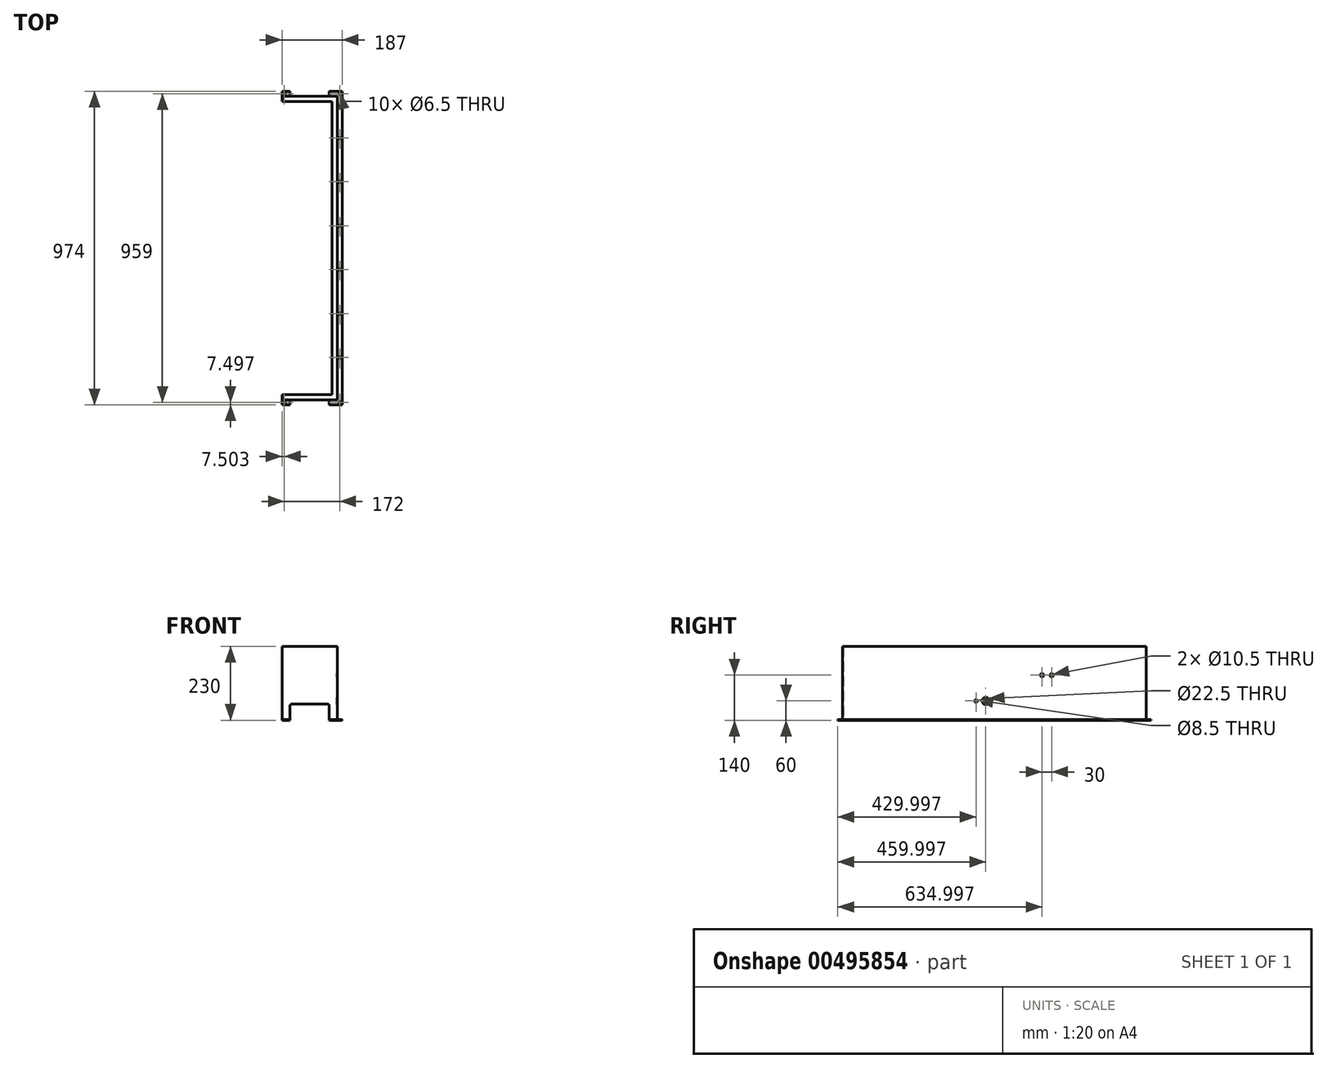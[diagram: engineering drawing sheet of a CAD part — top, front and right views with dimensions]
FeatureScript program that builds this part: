
annotation { "Feature Type Name" : "Feature", "Feature Type Description" : "" }
export const myFeature = defineFeature(function(context is Context, id is Id, definition is map)
    precondition{}
    {
        {
            var Q0;
            Q0=qCreatedBy(makeId("Top.planeOp"),FACE);
            var sketch = newSketch(context, id + "F0", { "sketchPlane" : qUnion([Q0])});
            skLineSegment(sketch, "E0", {"start": v(-19.6, 942) * mm, "end": v(150.4, 942) * mm});
            skLineSegment(sketch, "E1", {"start": v(150.4, 942) * mm, "end": v(150.4, 2) * mm});
            skLineSegment(sketch, "E2", {"start": v(150.4, 2) * mm, "end": v(-19.6, 2) * mm});
            skLineSegment(sketch, "E3", {"start": v(-19.6, 2) * mm, "end": v(-19.6, -15) * mm});
            skLineSegment(sketch, "E4", {"start": v(-19.6, -15) * mm, "end": v(167.4, -15) * mm});
            skLineSegment(sketch, "E5", {"start": v(167.4, -15) * mm, "end": v(167.4, 959) * mm});
            skLineSegment(sketch, "E6", {"start": v(167.4, 959) * mm, "end": v(-19.6, 959) * mm});
            skLineSegment(sketch, "E7", {"start": v(-19.6, 959) * mm, "end": v(-19.6, 942) * mm});
            skCircle(sketch, "E8", {"center": v(-12.1, 951.5) * mm, "radius": 3.25 * mm});
            skCircle(sketch, "E9", {"center": v(159.9, 951.5) * mm, "radius": 3.25 * mm});
            skCircle(sketch, "E10", {"center": v(-12.1, -7.5) * mm, "radius": 3.25 * mm});
            skCircle(sketch, "E11", {"center": v(159.9, -7.5) * mm, "radius": 3.25 * mm});
            skCircle(sketch, "E12.0.1.0", {"center": v(159.9, 814.9) * mm, "radius": 3.25 * mm});
            skCircle(sketch, "E12.0.2.0", {"center": v(159.9, 678.3) * mm, "radius": 3.25 * mm});
            skCircle(sketch, "E12.0.3.0", {"center": v(159.9, 541.7) * mm, "radius": 3.25 * mm});
            skCircle(sketch, "E12.0.4.0", {"center": v(159.9, 405.1) * mm, "radius": 3.25 * mm});
            skCircle(sketch, "E12.0.5.0", {"center": v(159.9, 268.5) * mm, "radius": 3.25 * mm});
            skCircle(sketch, "E12.0.6.0", {"center": v(159.9, 131.9) * mm, "radius": 3.25 * mm});
            skLineSegment(sketch, "E12.direction1", {"start": v(159.9, 951.5) * mm, "end": v(184.9, 951.5) * mm, "construction": true});
            skLineSegment(sketch, "E12.direction2", {"start": v(159.9, 951.5) * mm, "end": v(159.9, 814.9) * mm, "construction": true});
            skSolve(sketch);
        }
        {
            var Q0;
            Q0=qSketchRegion(id+"F0",true);
            extrude(context, id + "F1", {"entities" : qUnion([Q0]), "depth" : 2 * mm});
        }
        {
            var Q0;
            Q0=makeQuery(id+"F1.opExtrude","CAP_FACE",FACE,{"disambiguationData":[OSD([sQuery(id+"F0.wireOp",EDGE,"E0"),sQuery(id+"F0.wireOp",EDGE,"E1"),sQuery(id+"F0.wireOp",EDGE,"E2"),sQuery(id+"F0.wireOp",EDGE,"E3"),sQuery(id+"F0.wireOp",EDGE,"E4"),sQuery(id+"F0.wireOp",EDGE,"E5"),sQuery(id+"F0.wireOp",EDGE,"E6"),sQuery(id+"F0.wireOp",EDGE,"E7")])],"isStart":false});
            var sketch = newSketch(context, id + "F2", { "sketchPlane" : qUnion([Q0])});
            skLineSegment(sketch, "E13.0", {"start": v(-19.6, 942) * mm, "end": v(150.4, 942) * mm});
            skLineSegment(sketch, "E14.0", {"start": v(150.4, 942) * mm, "end": v(150.4, 2) * mm});
            skLineSegment(sketch, "E15.0", {"start": v(150.4, 2) * mm, "end": v(-19.6, 2) * mm});
            skLineSegment(sketch, "E16.0", {"start": v(152.4, 0) * mm, "end": v(-19.6, 0) * mm});
            skLineSegment(sketch, "E16.1", {"start": v(152.4, 944) * mm, "end": v(152.4, 0) * mm});
            skLineSegment(sketch, "E16.2", {"start": v(-19.6, 944) * mm, "end": v(152.4, 944) * mm});
            skLineSegment(sketch, "E17", {"start": v(-19.6, 0) * mm, "end": v(-19.6, 2) * mm});
            skLineSegment(sketch, "E18", {"start": v(-19.6, 944) * mm, "end": v(-19.6, 942) * mm});
            skSolve(sketch);
        }
        {
            var Q0;
            Q0=qSketchRegion(id+"F2",true);
            extrude(context, id + "F3", {"entities" : qUnion([Q0]), "operationType" : NewBodyOperationType.ADD, "depth" : 226 * mm});
        }
        {
            var Q0;
            Q0=makeQuery(id+"F3.opExtrude","CAP_FACE",FACE,{"disambiguationData":[OSD([sQuery(id+"F2.wireOp",EDGE,"E13.0"),sQuery(id+"F2.wireOp",EDGE,"E14.0"),sQuery(id+"F2.wireOp",EDGE,"E15.0"),sQuery(id+"F2.wireOp",EDGE,"E16.0"),sQuery(id+"F2.wireOp",EDGE,"E16.1"),sQuery(id+"F2.wireOp",EDGE,"E16.2"),sQuery(id+"F2.wireOp",EDGE,"E17"),sQuery(id+"F2.wireOp",EDGE,"E18")])],"isStart":false});
            var sketch = newSketch(context, id + "F4", { "sketchPlane" : qUnion([Q0])});
            skLineSegment(sketch, "E19.0", {"start": v(-19.6, 944) * mm, "end": v(152.4, 944) * mm});
            skLineSegment(sketch, "E20.0", {"start": v(152.4, 944) * mm, "end": v(152.4, 0) * mm});
            skLineSegment(sketch, "E21.0", {"start": v(152.4, 0) * mm, "end": v(-19.6, 0) * mm});
            skLineSegment(sketch, "E22.0", {"start": v(135.4, 17) * mm, "end": v(-19.6, 17) * mm});
            skLineSegment(sketch, "E22.1", {"start": v(135.4, 927) * mm, "end": v(135.4, 17) * mm});
            skLineSegment(sketch, "E22.2", {"start": v(-19.6, 927) * mm, "end": v(135.4, 927) * mm});
            skLineSegment(sketch, "E23", {"start": v(-19.6, 17) * mm, "end": v(-19.6, 0) * mm});
            skLineSegment(sketch, "E24", {"start": v(-19.6, 944) * mm, "end": v(-19.6, 927) * mm});
            skSolve(sketch);
        }
        {
            var Q0;
            Q0=qSketchRegion(id+"F4",true);
            extrude(context, id + "F5", {"entities" : qUnion([Q0]), "operationType" : NewBodyOperationType.ADD, "depth" : 2 * mm});
        }
        {
            var Q0;
            Q0=makeQuery(id+"F1.opExtrude","SWEPT_FACE",FACE,{"disambiguationData":[OSD([sQuery(id+"F0.wireOp",EDGE,"E6")])]});
            var sketch = newSketch(context, id + "F6", { "sketchPlane" : qUnion([Q0])});
            skLineSegment(sketch, "E25.bottom", {"start": v(-122.4, 50) * mm, "end": v(-10.4, 50) * mm});
            skLineSegment(sketch, "E25.top", {"start": v(-127.4, -20.45) * mm, "end": v(-5.4, -20.45) * mm});
            skLineSegment(sketch, "E25.left", {"start": v(-127.4, 45) * mm, "end": v(-127.4, -20.45) * mm});
            skLineSegment(sketch, "E25.right", {"start": v(-5.4, 45) * mm, "end": v(-5.4, -20.45) * mm});
            skPoint(sketch, "E26.visualSharp", {"position": v(-127.4, 50) * mm});
            skArc(sketch, "E26.filletArc", {"start": v(-122.4, 50) * mm, "mid": v(-125.93, 48.54) * mm, "end": v(-127.4, 45) * mm});
            skPoint(sketch, "E27.visualSharp", {"position": v(-5.4, 50) * mm});
            skArc(sketch, "E27.filletArc", {"start": v(-5.4, 45) * mm, "mid": v(-6.86, 48.54) * mm, "end": v(-10.4, 50) * mm});
            skSolve(sketch);
        }
        {
            var Q0;
            Q0=qSketchRegion(id+"F6",true);
            extrude(context, id + "F7", {"entities" : qUnion([Q0]), "operationType" : NewBodyOperationType.REMOVE, "oppositeDirection" : true, "depth" : 1221 * mm});
        }
        {
            var Q0;
            Q0=makeQuery(id+"F5.boolean.opBoolean","MERGE",FACE,{"derivedFrom":[makeQuery(id+"F3.opExtrude","SWEPT_FACE",FACE,{"disambiguationData":[OSD([sQuery(id+"F2.wireOp",EDGE,"E16.1")])]}),makeQuery(id+"F5.opExtrude","SWEPT_FACE",FACE,{"disambiguationData":[OSD([sQuery(id+"F4.wireOp",EDGE,"E20.0")])]})]});
            var sketch = newSketch(context, id + "F8", { "sketchPlane" : qUnion([Q0])});
            skCircle(sketch, "E28", {"center": v(620, 140) * mm, "radius": 5.25 * mm});
            skCircle(sketch, "E29", {"center": v(650, 140) * mm, "radius": 5.25 * mm});
            skCircle(sketch, "E30", {"center": v(445, 60) * mm, "radius": 11.25 * mm});
            skCircle(sketch, "E31", {"center": v(415, 60) * mm, "radius": 4.25 * mm});
            skSolve(sketch);
        }
        {
            var Q0;
            Q0=qSketchRegion(id+"F8",true);
            extrude(context, id + "F9", {"entities" : qUnion([Q0]), "operationType" : NewBodyOperationType.REMOVE, "oppositeDirection" : true, "depth" : 25 * mm});
        }
    });
